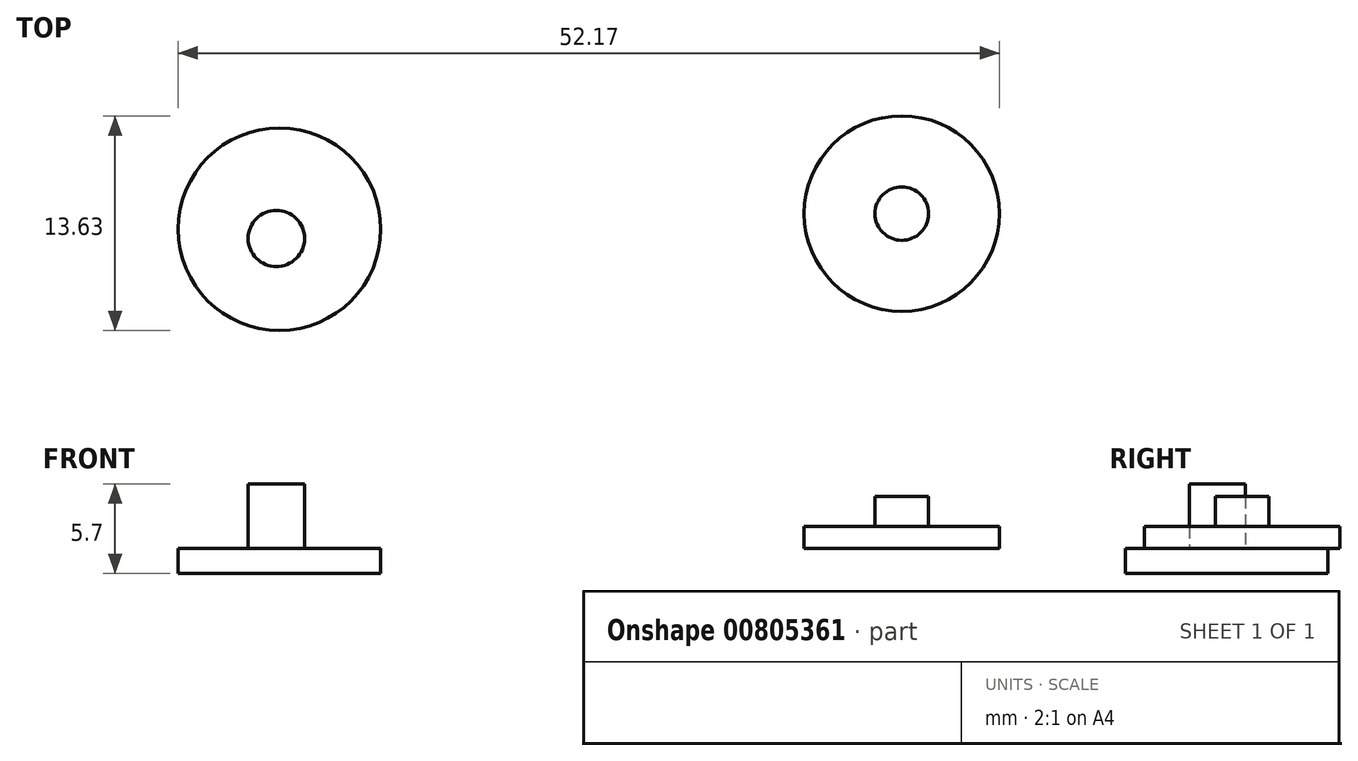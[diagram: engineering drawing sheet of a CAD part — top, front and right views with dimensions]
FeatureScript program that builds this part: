
annotation { "Feature Type Name" : "Feature", "Feature Type Description" : "" }
export const myFeature = defineFeature(function(context is Context, id is Id, definition is map)
    precondition{}
    {
        {
            var Q0;
            Q0=qCreatedBy(makeId("Top.planeOp"),FACE);
            var sketch = newSketch(context, id + "F0", { "sketchPlane" : qUnion([Q0])});
            skCircle(sketch, "E0", {"center": v(0.2, 0.6) * mm, "radius": 6.43 * mm});
            skSolve(sketch);
        }
        {
            var Q0;
            Q0=makeQuery(id+"F0.imprint","IMPRINT",FACE,{"disambiguationData":[TD([[makeQuery(id+"F0.imprint","IMPRINT",EDGE,{"derivedFrom":sQuery(id+"F0.wireOp",EDGE,"E0")}),1.0]])]});
            extrude(context, id + "F1", {"entities" : qUnion([Q0]), "depth" : 1.6 * mm, "offsetDistance" : 25 * mm});
        }
        {
            var Q0;
            Q0=makeQuery(id+"F1.opExtrude","CAP_FACE",FACE,{"disambiguationData":[OSD([sQuery(id+"F0.wireOp",EDGE,"E0")])],"isStart":false});
            var sketch = newSketch(context, id + "F2", { "sketchPlane" : qUnion([Q0])});
            skCircle(sketch, "E1", {"center": v(0, 0) * mm, "radius": 1.79 * mm});
            skSolve(sketch);
        }
        {
            var Q0;
            Q0 = qSketchRegion(id + "F2", true);
            extrude(context, id + "F3", {"entities" : qUnion([Q0]), "operationType" : NewBodyOperationType.ADD, "depth" : 4.1 * mm, "offsetDistance" : 25 * mm});
        }
        {
            var Q0;
            Q0=makeQuery(id+"F1.opExtrude","CAP_FACE",FACE,{"disambiguationData":[OSD([sQuery(id+"F0.wireOp",EDGE,"E0")])],"isStart":false});
            var sketch = newSketch(context, id + "F4", { "sketchPlane" : qUnion([Q0])});
            skCircle(sketch, "E2", {"center": v(39.72, 1.58) * mm, "radius": 6.2 * mm});
            skSolve(sketch);
        }
        {
            var Q0;
            Q0 = qSketchRegion(id + "F4", true);
            extrude(context, id + "F5", {"entities" : qUnion([Q0]), "depth" : 1.4 * mm, "offsetDistance" : 25 * mm});
        }
        {
            var Q0;
            Q0=makeQuery(id+"F5.opExtrude","CAP_FACE",FACE,{"disambiguationData":[OSD([sQuery(id+"F4.wireOp",EDGE,"E2")])],"isStart":false});
            var sketch = newSketch(context, id + "F6", { "sketchPlane" : qUnion([Q0])});
            skCircle(sketch, "E3", {"center": v(39.72, 1.58) * mm, "radius": 1.7 * mm});
            skSolve(sketch);
        }
        {
            var Q0;
            Q0=makeQuery(id+"F6.imprint","IMPRINT",FACE,{"disambiguationData":[TD([[makeQuery(id+"F6.imprint","IMPRINT",EDGE,{"derivedFrom":sQuery(id+"F6.wireOp",EDGE,"E3")}),1.0]])]});
            extrude(context, id + "F7", {"entities" : qUnion([Q0]), "operationType" : NewBodyOperationType.ADD, "depth" : 3.8 * mm, "offsetDistance" : 25 * mm});
        }
        {
            var Q0;
            Q0=makeQuery(id+"F7.opExtrude","CAP_FACE",FACE,{"disambiguationData":[OSD([sQuery(id+"F6.wireOp",EDGE,"E3")])],"isStart":false});
            extrude(context, id + "F8", {"entities" : qUnion([Q0]), "operationType" : NewBodyOperationType.REMOVE, "oppositeDirection" : true, "depth" : 1.9 * mm, "offsetDistance" : 25 * mm});
        }
    });
